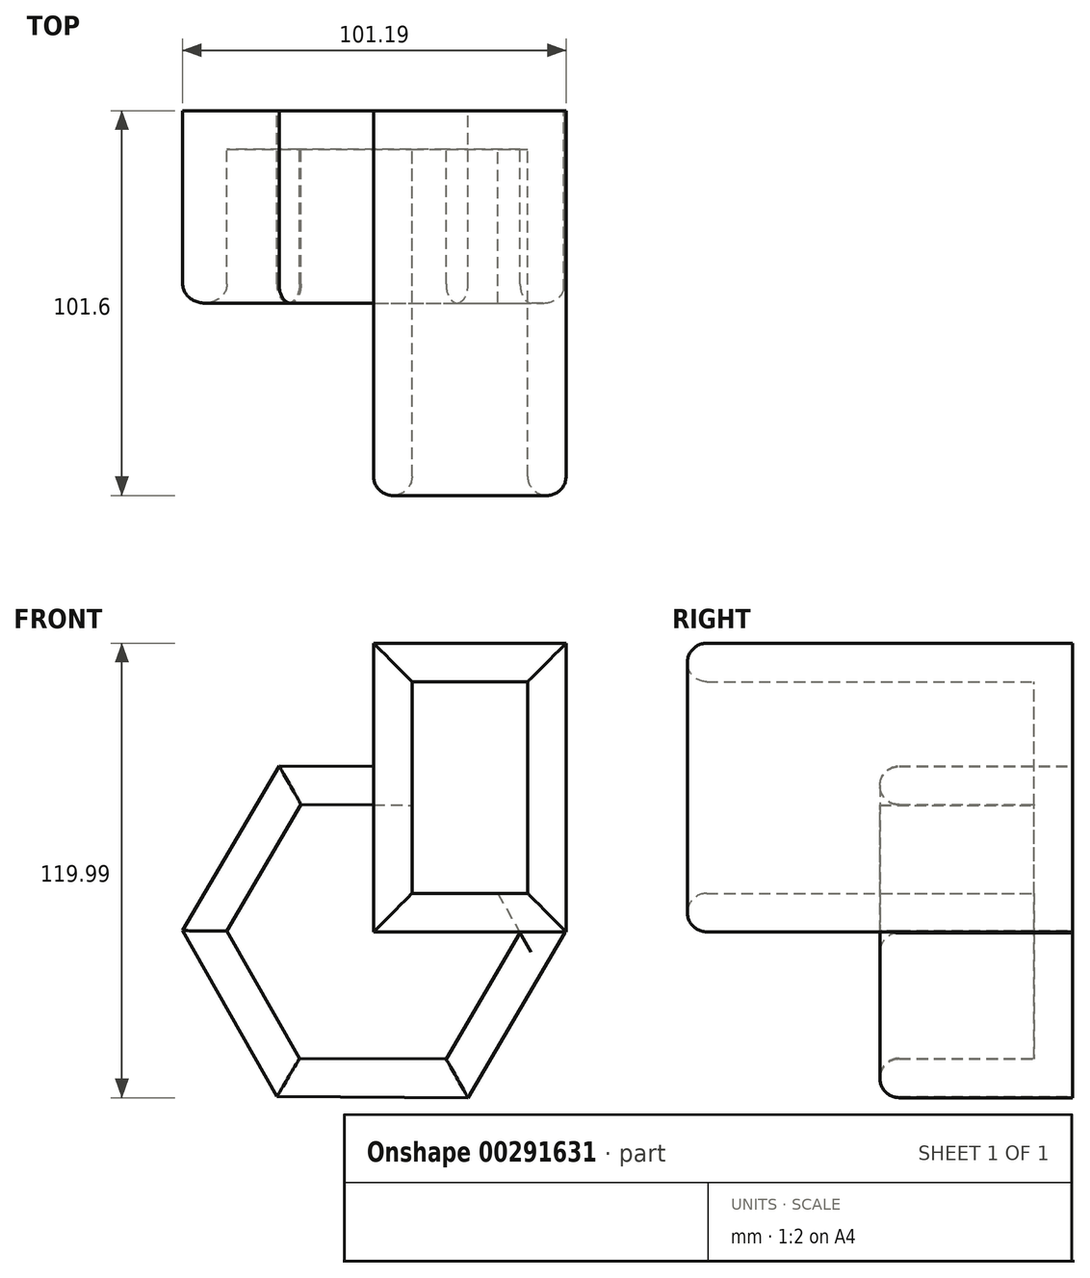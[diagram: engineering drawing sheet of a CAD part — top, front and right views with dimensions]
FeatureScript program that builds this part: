
annotation { "Feature Type Name" : "Feature", "Feature Type Description" : "" }
export const myFeature = defineFeature(function(context is Context, id is Id, definition is map)
    precondition{}
    {
        {
            var Q0;
            Q0=qCreatedBy(makeId("Front.planeOp"),FACE);
            var sketch = newSketch(context, id + "F0", { "sketchPlane" : qUnion([Q0])});
            skLineSegment(sketch, "E0.bottom", {"start": v(0, 0) * mm, "end": v(50.8, 0) * mm});
            skLineSegment(sketch, "E0.top", {"start": v(0, 76.2) * mm, "end": v(50.8, 76.2) * mm});
            skLineSegment(sketch, "E0.left", {"start": v(0, 0) * mm, "end": v(0, 76.2) * mm});
            skLineSegment(sketch, "E0.right", {"start": v(50.8, 0) * mm, "end": v(50.8, 76.2) * mm});
            skArc(sketch, "E1.cCircle", {"start": v(0.26, 43.64) * mm, "mid": v(-30.95, -30.77) * mm, "end": v(43.64, 0) * mm, "construction": true});
            skLineSegment(sketch, "E1.0", {"start": v(50.4, -0.3) * mm, "end": v(24.94, -43.8) * mm});
            skLineSegment(sketch, "E1.1", {"start": v(24.94, -43.8) * mm, "end": v(-25.46, -43.5) * mm});
            skLineSegment(sketch, "E1.2", {"start": v(-25.46, -43.5) * mm, "end": v(-50.4, 0.3) * mm});
            skLineSegment(sketch, "E1.3", {"start": v(-50.4, 0.3) * mm, "end": v(-24.94, 43.8) * mm});
            skLineSegment(sketch, "E1.4", {"start": v(-24.94, 43.8) * mm, "end": v(0.26, 43.64) * mm});
            skLineSegment(sketch, "E1.5", {"start": v(50.22, 0) * mm, "end": v(50.4, -0.3) * mm});
            skPoint(sketch, "E1.0.midPoint", {"position": v(37.67, -22.05) * mm});
            skPoint(sketch, "E2.orphan", {"position": v(25.46, 43.5) * mm});
            skSolve(sketch);
        }
        {
            var Q0;
            Q0=makeQuery(id+"F0.imprint","IMPRINT",FACE,{"disambiguationData":[TD([[makeQuery(id+"F0.imprint","IMPRINT",EDGE,{"derivedFrom":sQuery(id+"F0.wireOp",EDGE,"E0.bottom")}),1.0]])]});
            extrude(context, id + "F1", {"entities" : qUnion([Q0]), "depth" : 101.6 * mm});
        }
        {
            var Q0;
            Q0=makeQuery(id+"F0.imprint","IMPRINT",FACE,{"disambiguationData":[TD([[makeQuery(id+"F0.imprint","IMPRINT",EDGE,{"derivedFrom":sQuery(id+"F0.wireOp",EDGE,"E1.0")}),-1.0]])]});
            extrude(context, id + "F2", {"entities" : qUnion([Q0]), "operationType" : NewBodyOperationType.ADD, "depth" : 50.8 * mm});
        }
        {
            var Q0;
            Q0=makeQuery(id+"F1.opExtrude","CAP_FACE",FACE,{"disambiguationData":[OSD([sQuery(id+"F0.wireOp",EDGE,"E0.bottom"),sQuery(id+"F0.wireOp",EDGE,"E0.top"),sQuery(id+"F0.wireOp",EDGE,"E0.left"),sQuery(id+"F0.wireOp",EDGE,"E0.right")])],"isStart":false});
            var Q1;
            Q1=makeQuery(id+"F2.opExtrude","CAP_FACE",FACE,{"disambiguationData":[OSD([sQuery(id+"F0.wireOp",EDGE,"E0.bottom"),sQuery(id+"F0.wireOp",EDGE,"E0.left"),sQuery(id+"F0.wireOp",EDGE,"E1.0"),sQuery(id+"F0.wireOp",EDGE,"E1.1"),sQuery(id+"F0.wireOp",EDGE,"E1.2"),sQuery(id+"F0.wireOp",EDGE,"E1.3"),sQuery(id+"F0.wireOp",EDGE,"E1.4"),sQuery(id+"F0.wireOp",EDGE,"E1.5")])],"isStart":false});
            shell(context, id + "F3", {"entities" : qUnion([Q0, Q1]), "thickness" : 10.16 * mm});
        }
        {
            var Q0;
            {var subQ0=sQuery(id+"F0.wireOp",EDGE,"E0.top");Q0=makeQuery(id+"F3.opShell","OFFSET_EDGE",EDGE,{"disambiguationData":[OSD([subQ0]),TDD([makeQuery(id+"F1.opExtrude","CAP_EDGE",EDGE,{"disambiguationData":[OSD([subQ0])],"isStart":false})])]});}
            var Q1;
            {var subQ0=sQuery(id+"F0.wireOp",EDGE,"E0.right");Q1=makeQuery(id+"F3.opShell","OFFSET_EDGE",EDGE,{"disambiguationData":[OSD([subQ0]),TDD([makeQuery(id+"F1.opExtrude","CAP_EDGE",EDGE,{"disambiguationData":[OSD([subQ0])],"isStart":false})])]});}
            var Q2;
            {var subQ0=sQuery(id+"F0.wireOp",EDGE,"E0.bottom");Q2=makeQuery(id+"F3.opShell","OFFSET_EDGE",EDGE,{"disambiguationData":[OSD([subQ0]),TDD([makeQuery(id+"F1.opExtrude","CAP_EDGE",EDGE,{"disambiguationData":[OSD([subQ0])],"isStart":false})])]});}
            var Q3;
            {var subQ0=sQuery(id+"F0.wireOp",EDGE,"E0.left");Q3=makeQuery(id+"F3.opShell","OFFSET_EDGE",EDGE,{"disambiguationData":[OSD([subQ0]),TDD([makeQuery(id+"F1.opExtrude","CAP_EDGE",EDGE,{"disambiguationData":[OSD([subQ0])],"isStart":false})])]});}
            var Q4;
            {var subQ0=sQuery(id+"F0.wireOp",EDGE,"E1.4");Q4=makeQuery(id+"F3.opShell","OFFSET_EDGE",EDGE,{"disambiguationData":[OSD([subQ0]),TDD([makeQuery(id+"F2.opExtrude","CAP_EDGE",EDGE,{"disambiguationData":[OSD([subQ0])],"isStart":false})]),OD(0.0)]});}
            var Q5;
            {var subQ0=sQuery(id+"F0.wireOp",EDGE,"E1.3");Q5=makeQuery(id+"F3.opShell","OFFSET_EDGE",EDGE,{"disambiguationData":[OSD([subQ0]),TDD([makeQuery(id+"F2.opExtrude","CAP_EDGE",EDGE,{"disambiguationData":[OSD([subQ0])],"isStart":false})])]});}
            var Q6;
            {var subQ0=sQuery(id+"F0.wireOp",EDGE,"E1.2");Q6=makeQuery(id+"F3.opShell","OFFSET_EDGE",EDGE,{"disambiguationData":[OSD([subQ0]),TDD([makeQuery(id+"F2.opExtrude","CAP_EDGE",EDGE,{"disambiguationData":[OSD([subQ0])],"isStart":false})])]});}
            var Q7;
            {var subQ0=sQuery(id+"F0.wireOp",EDGE,"E1.1");Q7=makeQuery(id+"F3.opShell","OFFSET_EDGE",EDGE,{"disambiguationData":[OSD([subQ0]),TDD([makeQuery(id+"F2.opExtrude","CAP_EDGE",EDGE,{"disambiguationData":[OSD([subQ0])],"isStart":false})])]});}
            var Q8;
            {var subQ0=sQuery(id+"F0.wireOp",EDGE,"E1.0");Q8=makeQuery(id+"F3.opShell","OFFSET_EDGE",EDGE,{"disambiguationData":[OSD([subQ0]),TDD([makeQuery(id+"F2.opExtrude","CAP_EDGE",EDGE,{"disambiguationData":[OSD([subQ0])],"isStart":false})])]});}
            var Q9;
            Q9=makeQuery(id+"F2.opExtrude","CAP_EDGE",EDGE,{"disambiguationData":[OSD([sQuery(id+"F0.wireOp",EDGE,"E1.4")])],"isStart":false});
            var Q10;
            Q10=makeQuery(id+"F2.opExtrude","CAP_EDGE",EDGE,{"disambiguationData":[OSD([sQuery(id+"F0.wireOp",EDGE,"E1.3")])],"isStart":false});
            var Q11;
            Q11=makeQuery(id+"F2.opExtrude","CAP_EDGE",EDGE,{"disambiguationData":[OSD([sQuery(id+"F0.wireOp",EDGE,"E1.2")])],"isStart":false});
            var Q12;
            Q12=makeQuery(id+"F2.opExtrude","CAP_EDGE",EDGE,{"disambiguationData":[OSD([sQuery(id+"F0.wireOp",EDGE,"E1.1")])],"isStart":false});
            var Q13;
            Q13=makeQuery(id+"F2.opExtrude","CAP_EDGE",EDGE,{"disambiguationData":[OSD([sQuery(id+"F0.wireOp",EDGE,"E1.0")])],"isStart":false});
            var Q14;
            Q14=makeQuery(id+"F1.opExtrude","CAP_EDGE",EDGE,{"disambiguationData":[OSD([sQuery(id+"F0.wireOp",EDGE,"E0.left")])],"isStart":false});
            var Q15;
            Q15=makeQuery(id+"F1.opExtrude","CAP_EDGE",EDGE,{"disambiguationData":[OSD([sQuery(id+"F0.wireOp",EDGE,"E0.top")])],"isStart":false});
            var Q16;
            Q16=makeQuery(id+"F1.opExtrude","CAP_EDGE",EDGE,{"disambiguationData":[OSD([sQuery(id+"F0.wireOp",EDGE,"E0.right")])],"isStart":false});
            var Q17;
            Q17=makeQuery(id+"F1.opExtrude","CAP_EDGE",EDGE,{"disambiguationData":[OSD([sQuery(id+"F0.wireOp",EDGE,"E0.bottom")])],"isStart":false});
            fillet(context, id + "F4", {"entities" : qUnion([Q0, Q1, Q2, Q3, Q4, Q5, Q6, Q7, Q8, Q9, Q10, Q11, Q12, Q13, Q14, Q15, Q16, Q17]), "radius" : 5.08 * mm, "tangentPropagation" : true, "allowEdgeOverflow" : false});
        }
    });
